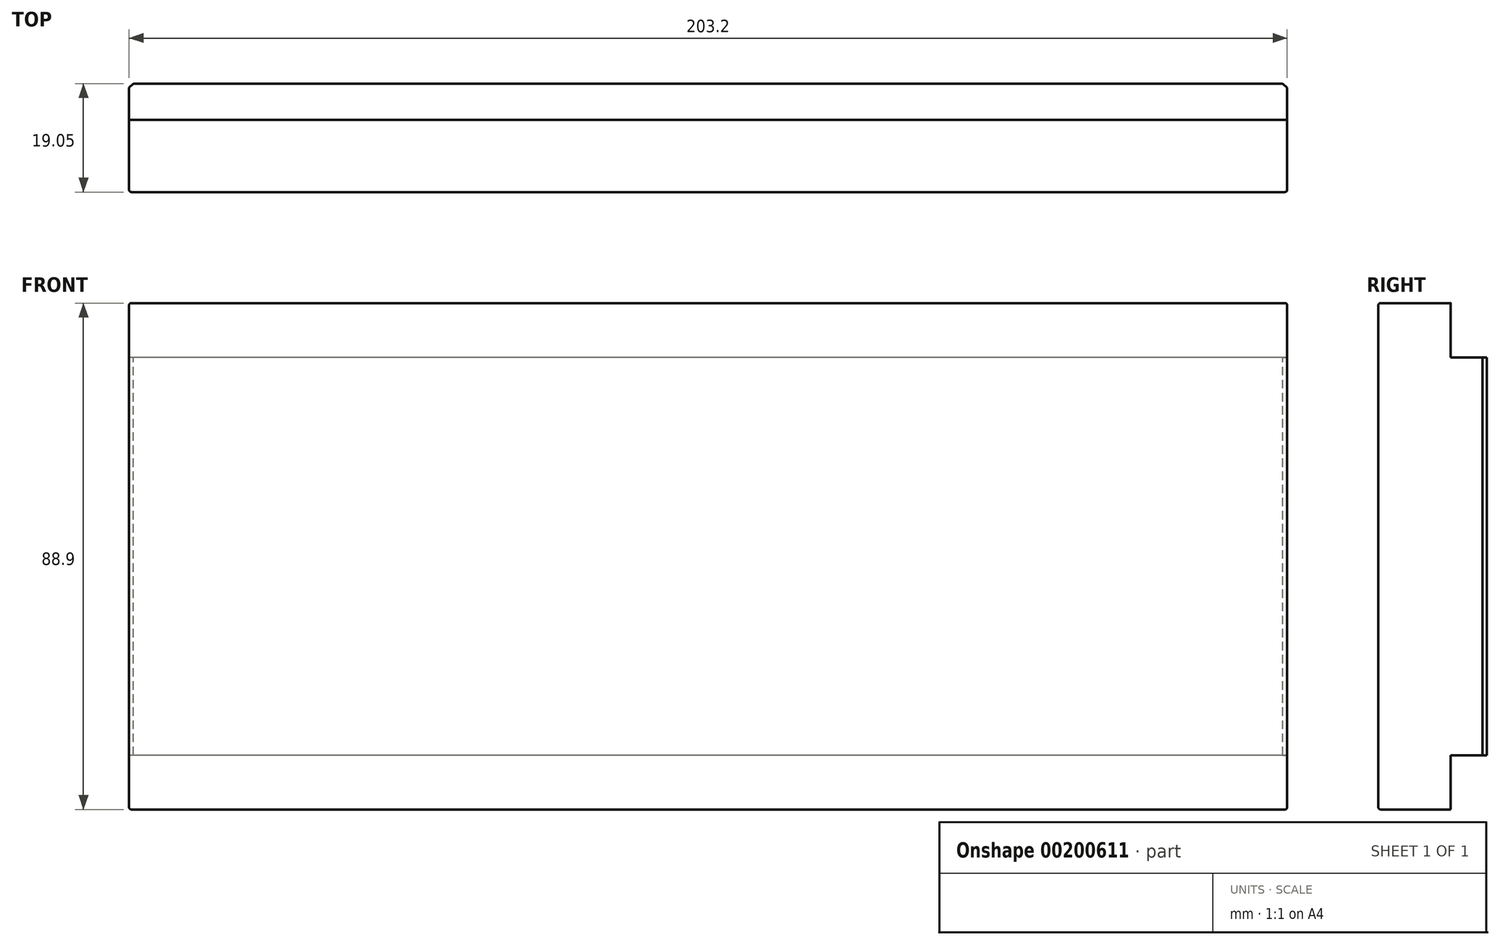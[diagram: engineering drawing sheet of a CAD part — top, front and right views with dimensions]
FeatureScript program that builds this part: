
annotation { "Feature Type Name" : "Feature", "Feature Type Description" : "" }
export const myFeature = defineFeature(function(context is Context, id is Id, definition is map)
    precondition{}
    {
        {
            assignVariable(context, id + "F0", {"name" : "width", "anyValue" : 0.75});
        }
        {
            var Q0;
            Q0=qCreatedBy(makeId("Right.planeOp"),FACE);
            var sketch = newSketch(context, id + "F1", { "sketchPlane" : qUnion([Q0])});
            skLineSegment(sketch, "E0.top", {"start": v(-6.35, 34.93) * mm, "end": v(0, 34.93) * mm});
            skLineSegment(sketch, "E0.left", {"start": v(-6.35, 44.45) * mm, "end": v(-6.35, 34.93) * mm});
            skLineSegment(sketch, "E1.bottom", {"start": v(0, 0) * mm, "end": v(-19.05, 0) * mm});
            skLineSegment(sketch, "E2", {"start": v(-19.05, 44.45) * mm, "end": v(-19.05, 0) * mm});
            skLineSegment(sketch, "E3", {"start": v(-19.05, 44.45) * mm, "end": v(-6.35, 44.45) * mm});
            skLineSegment(sketch, "E4", {"start": v(0, 34.93) * mm, "end": v(0, 0) * mm});
            skSolve(sketch);
        }
        {
            var Q0;
            Q0=makeQuery(id+"F1.imprint","IMPRINT",FACE,{"disambiguationData":[TD([[makeQuery(id+"F1.imprint","IMPRINT",EDGE,{"derivedFrom":sQuery(id+"F1.wireOp",EDGE,"E0.top")}),-1.0]])]});
            var Q1;
            Q1=makeQuery(id+"F1.imprint","IMPRINT",FACE,{"disambiguationData":[TD([[makeQuery(id+"F1.imprint","IMPRINT",EDGE,{"derivedFrom":sQuery(id+"F1.wireOp",EDGE,"E1.bottom")}),1.0]])]});
            extrude(context, id + "F2", {"entities" : qUnion([Q0, Q1]), "depth" : 101.6 * mm});
        }
        {
            var Q0;
            {var subQ0=makeQuery(id+"F4.opChamfer","BLEND_EDGE",EDGE,{"blendedFrom":[makeQuery(id+"F2.opExtrude","CAP_EDGE",EDGE,{"disambiguationData":[OSD([sQuery(id+"F1.wireOp",EDGE,"E4")])],"isStart":true}),makeQuery(id+"F2.opExtrude","SWEPT_FACE",FACE,{"disambiguationData":[OSD([sQuery(id+"F1.wireOp",EDGE,"E2")])]})],"blendedInto":[makeQuery(id+"F2.opExtrude","SWEPT_FACE",FACE,{"disambiguationData":[OSD([sQuery(id+"F1.wireOp",EDGE,"E2")])]})]});Q0=makeQuery(id+"F7.boolean.opBoolean","MERGE",EDGE,{"derivedFrom":[subQ0,makeQuery(id+"F7.opPattern","COPY",EDGE,{"derivedFrom":subQ0,"instanceName":"1"})]});}
            var Q1;
            Q1=makeQuery(id+"F2.opExtrude","CAP_EDGE",EDGE,{"disambiguationData":[OSD([sQuery(id+"F1.wireOp",EDGE,"E2")])],"isStart":true});
            fillet(context, id + "F3", {"entities" : qUnion([Q0, Q1]), "radius" : (getVariable(context, 'width') / 2) * mm, "tangentPropagation" : true, "allowEdgeOverflow" : false});
        }
        {
            var Q0;
            Q0=makeQuery(id+"F2.opExtrude","CAP_EDGE",EDGE,{"disambiguationData":[OSD([sQuery(id+"F1.wireOp",EDGE,"E4"),sQuery(id+"F1.wireOp",EDGE,"06acdf28-0093-4394-9228-6f8524038c1c4.MirrorCS")])],"isStart":true});
            chamfer(context, id + "F4", {"entities" : qUnion([Q0]), "width" : (getVariable(context, 'width')) * mm, "tangentPropagation" : true});
        }
        {
            var Q0;
            Q0=makeQuery(id+"F2.opExtrude","SWEPT_BODY",BODY,{"disambiguationData":[OSD([sQuery(id+"F1.wireOp",EDGE,"E0.top"),sQuery(id+"F1.wireOp",EDGE,"E0.left"),sQuery(id+"F1.wireOp",EDGE,"E2"),sQuery(id+"F1.wireOp",EDGE,"E3"),sQuery(id+"F1.wireOp",EDGE,"E4"),sQuery(id+"F1.wireOp",EDGE,"06acdf28-0093-4394-9228-6f8524038c1c0.MirrorCS"),sQuery(id+"F1.wireOp",EDGE,"06acdf28-0093-4394-9228-6f8524038c1c1.MirrorCS"),sQuery(id+"F1.wireOp",EDGE,"06acdf28-0093-4394-9228-6f8524038c1c2.MirrorCS"),sQuery(id+"F1.wireOp",EDGE,"06acdf28-0093-4394-9228-6f8524038c1c3.MirrorCS"),sQuery(id+"F1.wireOp",EDGE,"06acdf28-0093-4394-9228-6f8524038c1c4.MirrorCS")])]});
            var Q1;
            Q1=makeQuery(id+"F2.opExtrude","CAP_FACE",FACE,{"disambiguationData":[OSD([sQuery(id+"F1.wireOp",EDGE,"E0.top"),sQuery(id+"F1.wireOp",EDGE,"E0.left"),sQuery(id+"F1.wireOp",EDGE,"E2"),sQuery(id+"F1.wireOp",EDGE,"E3"),sQuery(id+"F1.wireOp",EDGE,"E4"),sQuery(id+"F1.wireOp",EDGE,"06acdf28-0093-4394-9228-6f8524038c1c0.MirrorCS"),sQuery(id+"F1.wireOp",EDGE,"06acdf28-0093-4394-9228-6f8524038c1c1.MirrorCS"),sQuery(id+"F1.wireOp",EDGE,"06acdf28-0093-4394-9228-6f8524038c1c2.MirrorCS"),sQuery(id+"F1.wireOp",EDGE,"06acdf28-0093-4394-9228-6f8524038c1c3.MirrorCS"),sQuery(id+"F1.wireOp",EDGE,"06acdf28-0093-4394-9228-6f8524038c1c4.MirrorCS")])],"isStart":false});
            mirror(context, id + "F5", {"operationType" : NewBodyOperationType.ADD, "entities" : qUnion([Q0]), "mirrorPlane" : qUnion([Q1])});
        }
        {
            var Q0;
            {var subQ0=makeQuery(id+"F2.opExtrude","SWEPT_EDGE",EDGE,{"disambiguationData":[OSD([sQuery(id+"F1.wireOp",EDGE,"E2"),sQuery(id+"F1.wireOp",EDGE,"E3")])]});Q0=makeQuery(id+"F5.boolean.opBoolean","MERGE",EDGE,{"derivedFrom":[subQ0,makeQuery(id+"F5.opPattern","COPY",EDGE,{"derivedFrom":subQ0,"instanceName":"1"})]});}
            fillet(context, id + "F6", {"entities" : qUnion([Q0]), "radius" : (getVariable(context, 'width') / 2) * mm, "tangentPropagation" : true, "allowEdgeOverflow" : false});
        }
        {
            var Q0;
            Q0=makeQuery(id+"F2.opExtrude","SWEPT_BODY",BODY,{"disambiguationData":[OSD([sQuery(id+"F1.wireOp",EDGE,"E0.top"),sQuery(id+"F1.wireOp",EDGE,"E0.left"),sQuery(id+"F1.wireOp",EDGE,"E1.bottom"),sQuery(id+"F1.wireOp",EDGE,"E2"),sQuery(id+"F1.wireOp",EDGE,"E3"),sQuery(id+"F1.wireOp",EDGE,"E4")])]});
            var Q1;
            {var subQ0=makeQuery(id+"F2.opExtrude","SWEPT_FACE",FACE,{"disambiguationData":[OSD([sQuery(id+"F1.wireOp",EDGE,"E1.bottom")])]});Q1=makeQuery(id+"F5.boolean.opBoolean","MERGE",FACE,{"derivedFrom":[subQ0,makeQuery(id+"F5.opPattern","COPY",FACE,{"derivedFrom":subQ0,"instanceName":"1"})]});}
            mirror(context, id + "F7", {"operationType" : NewBodyOperationType.ADD, "entities" : qUnion([Q0]), "mirrorPlane" : qUnion([Q1])});
        }
    });
